# Revit family: РИДАН_Автоматический клапан AQT-R3
name_source: partatom
category: Арматура трубопроводов
units: mm (PartAtom-declared; Revit-internal decimal feet)

## family parameters
Всегда вертикально = Да
На основе рабочей плоскости = Нет
Общий = Нет
При загрузке вырезать с полостями = Нет
Размер круглого соединителя = Использовать диаметр
Тип детали = Вставляется

## types (8) — shared parameters
ADSK_Версия Revit = 2019
ADSK_Версия семейства = 1.0
ADSK_Единица измерения = шт.
ADSK_Завод-изготовитель = ООО «Ридан-Трейд»
ADSK_Количество = 1
ADSK_Расход жидкости = 0.0 л/с
LT = APQT
URL = https://ridan.ru
b = 2 мм
Изготовитель = Ридан
Ниппели = Нет
zero-valued in all types: nip

## per-type parameters (varying)
| type | ADSK_Диаметр условный | ADSK_Код изделия | ADSK_Марка | ADSK_Масса | ADSK_Наименование | DP | HP | a | c | d | e | f | g | h |
| DN 15 | 15 мм | 003Z1402R | APQT DN15 | 0.42 | Автоматический комбинированный балансировочный клапан APQT PN16, Tmax=120C, DN15 | 20 мм | 0 | 6 мм | 51 мм | 24 мм | 4 мм | 26 мм | 23 мм | 67 мм |
| DN 15 HP | 15 мм | 003Z1412R | APQT DN15 HP | 0.42 | Автоматический комбинированный балансировочный клапан APQT PN16, Tmax=120C, DN15 HP | 20 мм | 1 | 6 мм | 51 мм | 24 мм | 4 мм | 26 мм | 23 мм | 67 мм |
| DN 20 | 20 мм | 003Z1403R | APQT DN20 | 0.63 | Автоматический комбинированный балансировочный клапан APQT PN16, Tmax=120C, DN20 | 25 мм | 0 | 8 мм | 64 мм | 31 мм | 5 мм | 33 мм | 30 мм | 84 мм |
| DN 25 | 25 мм | 003Z1404R | APQT DN25 | 1.21 | Автоматический комбинированный балансировочный клапан APQT PN16, Tmax=120C, DN25 | 32 мм | 0 | 10 мм | 82 мм | 40 мм | 6 мм | 42 мм | 39 мм | 106 мм |
| DN 32 | 32 мм | 003Z1405R | APQT DN32 | 2.14 | Автоматический комбинированный балансировочный клапан APQT PN16, Tmax=120C, DN32 | 40 мм | 0 | 12 мм | 103 мм | 51 мм | 7 мм | 48 мм | 44 мм | 130 мм |
| DN 20 HP | 20 мм | 003Z1413R | APQT DN20 HP | 0.63 | Автоматический комбинированный балансировочный клапан APQT PN16, Tmax=120C, DN20 HP | 25 мм | 1 | 8 мм | 64 мм | 31 мм | 5 мм | 33 мм | 30 мм | 84 мм |
| DN 25 HP | 25 мм | 003Z1414R | APQT DN25 HP | 1.21 | Автоматический комбинированный балансировочный клапан APQT PN16, Tmax=120C, DN25 HP | 32 мм | 1 | 10 мм | 82 мм | 40 мм | 6 мм | 42 мм | 39 мм | 106 мм |
| DN 32 HP | 32 мм | 003Z1415R | APQT DN32 HP | 2.14 | Автоматический комбинированный балансировочный клапан APQT PN16, Tmax=120C, DN32 HP | 40 мм | 1 | 12 мм | 103 мм | 51 мм | 7 мм | 48 мм | 44 мм | 130 мм |
